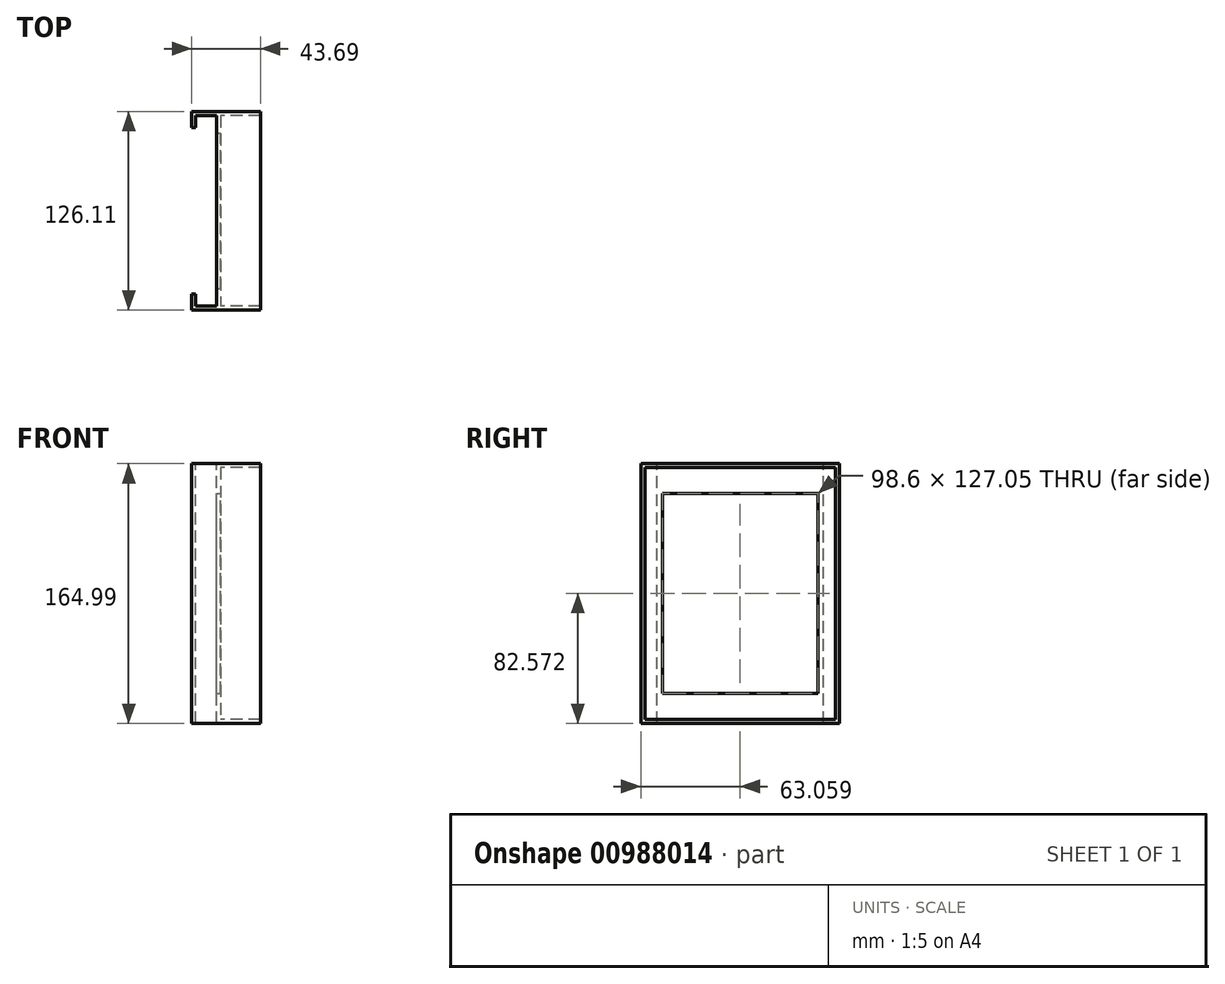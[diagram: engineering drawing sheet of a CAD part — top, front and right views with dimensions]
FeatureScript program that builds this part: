
annotation { "Feature Type Name" : "Feature", "Feature Type Description" : "" }
export const myFeature = defineFeature(function(context is Context, id is Id, definition is map)
    precondition{}
    {
        {
            var Q0;
            Q0=qCreatedBy(makeId("Right.planeOp"),FACE);
            var sketch = newSketch(context, id + "F0", { "sketchPlane" : qUnion([Q0])});
            skLineSegment(sketch, "E0.bottom", {"start": v(87.63, 67.2) * mm, "end": v(-33.4, 67.2) * mm});
            skLineSegment(sketch, "E0.top", {"start": v(87.63, -92.72) * mm, "end": v(-33.4, -92.72) * mm});
            skLineSegment(sketch, "E0.left", {"start": v(87.63, 67.2) * mm, "end": v(87.63, -92.72) * mm});
            skLineSegment(sketch, "E0.right", {"start": v(-33.4, 67.2) * mm, "end": v(-33.4, -92.72) * mm});
            skLineSegment(sketch, "E1.0", {"start": v(90.17, 69.73) * mm, "end": v(90.17, -95.26) * mm});
            skLineSegment(sketch, "E1.1", {"start": v(90.17, 69.73) * mm, "end": v(-35.94, 69.73) * mm});
            skLineSegment(sketch, "E1.2", {"start": v(-35.94, 69.73) * mm, "end": v(-35.94, -95.26) * mm});
            skLineSegment(sketch, "E1.3", {"start": v(90.17, -95.26) * mm, "end": v(-35.94, -95.26) * mm});
            skSolve(sketch);
        }
        {
            var Q0;
            Q0=makeQuery(id+"F0.imprint","IMPRINT",FACE,{"disambiguationData":[TD([[makeQuery(id+"F0.imprint","IMPRINT",EDGE,{"derivedFrom":sQuery(id+"F0.wireOp",EDGE,"E0.bottom")}),-1.0]])]});
            extrude(context, id + "F1", {"entities" : qUnion([Q0]), "depth" : 25.4 * mm, "offsetDistance" : 25.4 * mm});
        }
        {
            var Q0;
            Q0=makeQuery(id+"F1.opExtrude","CAP_FACE",FACE,{"disambiguationData":[OSD([sQuery(id+"F0.wireOp",EDGE,"E0.bottom"),sQuery(id+"F0.wireOp",EDGE,"E0.top"),sQuery(id+"F0.wireOp",EDGE,"E0.left"),sQuery(id+"F0.wireOp",EDGE,"E0.right"),sQuery(id+"F0.wireOp",EDGE,"E1.0"),sQuery(id+"F0.wireOp",EDGE,"E1.1"),sQuery(id+"F0.wireOp",EDGE,"E1.2"),sQuery(id+"F0.wireOp",EDGE,"E1.3")])],"isStart":true});
            var Q1;
            Q1 = qSketchRegion(id + "F0", true);
            var Q2;
            Q2=makeQuery(id+"F0.imprint","IMPRINT",FACE,{"disambiguationData":[TD([[makeQuery(id+"F0.imprint","IMPRINT",EDGE,{"derivedFrom":sQuery(id+"F0.wireOp",EDGE,"E0.bottom")}),1.0]])]});
            extrude(context, id + "F2", {"entities" : qUnion([Q0, Q1, Q2]), "operationType" : NewBodyOperationType.ADD, "depth" : 2.54 * mm, "offsetDistance" : 25.4 * mm});
        }
        {
            var Q0;
            {var subQ0=sQuery(id+"F0.wireOp",EDGE,"E1.1");Q0=makeQuery(id+"F2.boolean.opBoolean","MERGE",FACE,{"derivedFrom":[makeQuery(id+"F1.opExtrude","SWEPT_FACE",FACE,{"disambiguationData":[OSD([subQ0])]}),makeQuery(id+"F2.opExtrude","SWEPT_FACE",FACE,{"disambiguationData":[OSD([subQ0]),TDD([makeQuery(id+"F0.imprint","IMPRINT",EDGE,{"derivedFrom":subQ0})])]})]});}
            var sketch = newSketch(context, id + "F3", { "sketchPlane" : qUnion([Q0])});
            skLineSegment(sketch, "E2", {"start": v(-2.54, 90.17) * mm, "end": v(-18.29, 90.17) * mm});
            skLineSegment(sketch, "E3", {"start": v(-18.29, 90.17) * mm, "end": v(-18.29, 80.01) * mm});
            skLineSegment(sketch, "E4", {"start": v(-18.29, 80.01) * mm, "end": v(-15.75, 80.01) * mm});
            skLineSegment(sketch, "E5", {"start": v(-15.75, 80.01) * mm, "end": v(-15.75, 87.63) * mm});
            skLineSegment(sketch, "E6", {"start": v(-15.75, 87.63) * mm, "end": v(-2.54, 87.63) * mm});
            skLineSegment(sketch, "E7", {"start": v(-2.54, 87.63) * mm, "end": v(-2.54, 90.17) * mm});
            skLineSegment(sketch, "E8", {"start": v(-2.54, -35.94) * mm, "end": v(-18.29, -35.94) * mm});
            skLineSegment(sketch, "E9", {"start": v(-18.29, -35.94) * mm, "end": v(-18.29, -25.78) * mm});
            skLineSegment(sketch, "E10", {"start": v(-18.29, -25.78) * mm, "end": v(-15.75, -25.78) * mm});
            skLineSegment(sketch, "E11", {"start": v(-15.75, -25.78) * mm, "end": v(-15.75, -33.4) * mm});
            skLineSegment(sketch, "E12", {"start": v(-15.75, -33.4) * mm, "end": v(-2.54, -33.4) * mm});
            skLineSegment(sketch, "E13", {"start": v(-2.54, -33.4) * mm, "end": v(-2.54, -33.4) * mm});
            skSolve(sketch);
        }
        {
            var Q0;
            Q0=makeQuery(id+"F3.imprint","IMPRINT",FACE,{"disambiguationData":[TD([[makeQuery(id+"F3.imprint","IMPRINT",EDGE,{"derivedFrom":sQuery(id+"F3.wireOp",EDGE,"E2")}),1.0]])]});
            var Q1;
            {var subQ0=sQuery(id+"F3.wireOp",EDGE,"E8");Q1=makeQuery(id+"F3.imprint","IMPRINT",FACE,{"disambiguationData":[TD([[makeQuery(id+"F3.imprint","IMPRINT",EDGE,{"derivedFrom":subQ0}),-1.0]])]});}
            extrude(context, id + "F4", {"entities" : qUnion([Q0, Q1]), "operationType" : NewBodyOperationType.ADD, "depth" : -165 * mm, "offsetDistance" : 25.4 * mm});
        }
        {
            var Q0;
            Q0=makeQuery(id+"F2.opExtrude","CAP_FACE",FACE,{"disambiguationData":[OSD([sQuery(id+"F0.wireOp",EDGE,"E1.0"),sQuery(id+"F0.wireOp",EDGE,"E1.1"),sQuery(id+"F0.wireOp",EDGE,"E1.2"),sQuery(id+"F0.wireOp",EDGE,"E1.3")])],"isStart":true});
            var sketch = newSketch(context, id + "F5", { "sketchPlane" : qUnion([Q0])});
            skLineSegment(sketch, "E14.bottom", {"start": v(-22.18, -76.21) * mm, "end": v(76.42, -76.21) * mm});
            skLineSegment(sketch, "E14.top", {"start": v(-22.18, 50.84) * mm, "end": v(76.42, 50.84) * mm});
            skLineSegment(sketch, "E14.left", {"start": v(-22.18, -76.21) * mm, "end": v(-22.18, 50.84) * mm});
            skLineSegment(sketch, "E14.right", {"start": v(76.42, -76.21) * mm, "end": v(76.42, 50.84) * mm});
            skSolve(sketch);
        }
        {
            var Q0;
            Q0=makeQuery(id+"F5.imprint","IMPRINT",FACE,{"disambiguationData":[TD([[makeQuery(id+"F5.imprint","IMPRINT",EDGE,{"derivedFrom":sQuery(id+"F5.wireOp",EDGE,"E14.bottom")}),1.0]])]});
            extrude(context, id + "F6", {"entities" : qUnion([Q0]), "operationType" : NewBodyOperationType.REMOVE, "oppositeDirection" : true, "depth" : 25.4 * mm, "offsetDistance" : 25.4 * mm});
        }
    });
